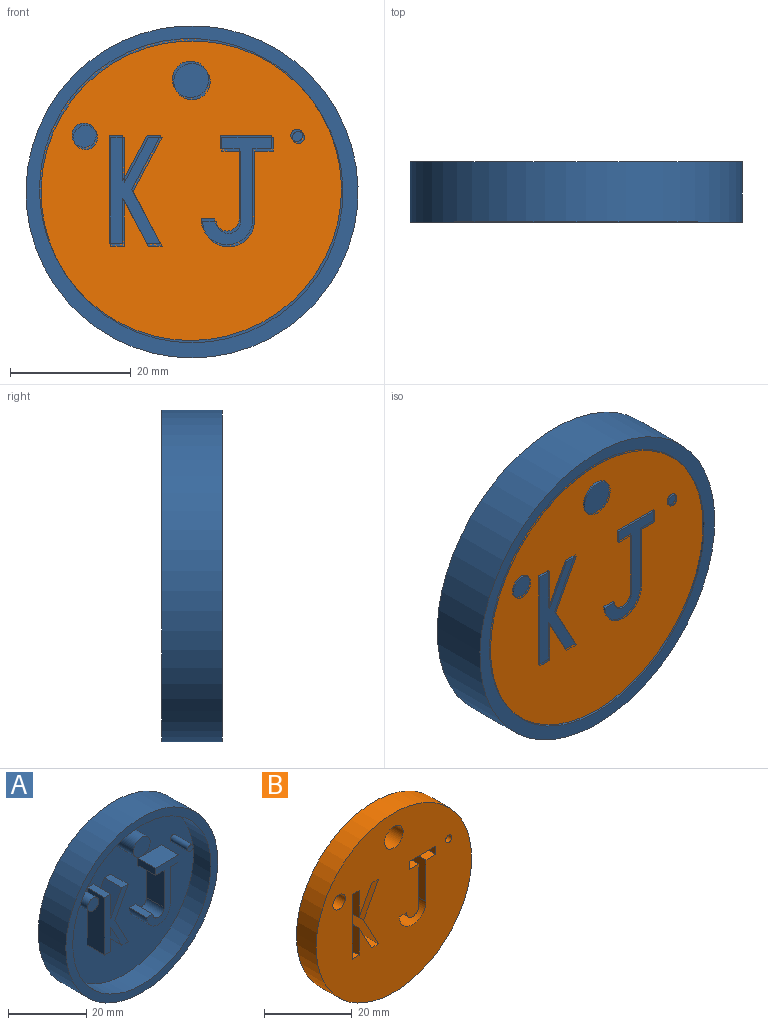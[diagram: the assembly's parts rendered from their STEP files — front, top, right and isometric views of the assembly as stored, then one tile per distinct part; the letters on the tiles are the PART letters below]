
ASSEMBLY  parts=2 mates=1
PART A: 34 faces, bbox 55x10x55 mm
  f0: cylinder r=25mm len=50mm, axis (0,1,0), area 997.5mm2, adj f2,f33
  f1: cylinder r=27.5mm len=55mm, axis (0,1,0), area 1727.9mm2, adj f2,f3
  f2: plane 55x55mm, normal (0,-1,0), area 412.3mm2, adj f0,f1
  f3: plane 55x55mm, normal (0,1,0), area 2375.8mm2, adj f1
  f4: cylinder r=2mm len=6.35mm, axis (0,1,0), area 79.8mm2, adj f5,f33
  f5: plane 4x4mm, normal (0,-1,0), area 12.6mm2, adj f4
  f6: cylinder r=3mm len=6.35mm, axis (0,1,0), area 119.7mm2, adj f7,f33
  f7: plane 6x6mm, normal (0,-1,0), area 28.3mm2, adj f6
  f8: cylinder r=1mm len=6.35mm, axis (0,1,0), area 39.9mm2, adj f9,f33
  f9: plane 2x2mm, normal (0,-1,0), area 3.1mm2, adj f8
  f10: plane 6.35x2.25mm, normal (0,0,1), area 14.3mm2, adj f11,f20,f21,f33
  f11: plane 18x6.35mm, normal (-1,0,0), area 114.3mm2, adj f10,f12,f21,f33
  f12: plane 6.35x2.25mm, normal (0,0,-1), area 14.3mm2, adj f11,f13,f21,f33
  f13: plane 7.5x6.35mm, normal (1,0,0), area 47.6mm2, adj f12,f14,f21,f33
  f14: plane 7.5x6.35mm, normal (-0.88,0,-0.47), area 54mm2, adj f13,f15,f21,f33
  f15: plane 6.35x2.25mm, normal (0,0,-1), area 14.3mm2, adj f14,f16,f21,f33
  f16: plane 9x6.35mm, normal (0.88,0,0.47), area 64.8mm2, adj f15,f17,f21,f33
  f17: plane 9x6.35mm, normal (0.88,0,-0.47), area 64.8mm2, adj f16,f18,f21,f33
  f18: plane 6.35x2.25mm, normal (0,0,1), area 14.3mm2, adj f17,f19,f21,f33
  f19: plane 7.5x6.35mm, normal (-0.88,0,0.47), area 54mm2, adj f18,f20,f21,f33
  f20: plane 7.5x6.35mm, normal (1,0,0), area 47.6mm2, adj f10,f19,f21,f33
  f21: plane 18x8.5mm, normal (0,-1,0), area 79.8mm2, adj f10,f11,f12,f13,f14,f15,f16,f17
  f22: plane 8.5x6.35mm, normal (0,0,1), area 54mm2, adj f23,f31,f32,f33
  f23: plane 6.35x2.25mm, normal (-1,0,0), area 14.3mm2, adj f22,f24,f32,f33
  f24: plane 6.35x3.13mm, normal (0,0,-1), area 19.8mm2, adj f23,f25,f32,f33
  f25: plane 11.6x6.35mm, normal (-1,0,0), area 73.7mm2, adj f24,f26,f32,f33
  f26: cylinder r=2.02mm len=6.35mm, axis (0,1,0), area 40.4mm2, adj f25,f27,f32,f33
  f27: plane 6.35x2.25mm, normal (0,0,1), area 14.3mm2, adj f26,f28,f32,f33
  f28: cylinder r=4.27mm len=8.55mm, axis (0,1,0), area 85.3mm2, adj f27,f29,f32,f33
  f29: plane 11.6x6.35mm, normal (1,0,0), area 73.7mm2, adj f28,f30,f32,f33
  f30: plane 6.35x3.13mm, normal (0,0,-1), area 19.8mm2, adj f29,f31,f32,f33
  f31: plane 6.35x2.25mm, normal (1,0,0), area 14.3mm2, adj f22,f30,f32,f33
  f32: plane 18.13x11.67mm, normal (0,-1,0), area 67.5mm2, adj f22,f23,f24,f25,f26,f27,f28,f29
  f33: plane 50x50mm, normal (0,-1,0), area 1772.2mm2, adj f0,f4,f6,f8,f10,f11,f12,f13
PART B: 27 faces, bbox 50x6.4x50 mm
  f0: plane 6.35x2.25mm, normal (1,0,0), area 14.3mm2, adj f1,f24,f25,f26
  f1: plane 8.5x6.35mm, normal (0,0,-1), area 54mm2, adj f0,f2,f25,f26
  f2: plane 6.35x2.25mm, normal (-1,0,0), area 14.3mm2, adj f1,f3,f25,f26
  f3: plane 6.35x3.13mm, normal (0,0,1), area 19.8mm2, adj f2,f4,f25,f26
  f4: plane 11.6x6.35mm, normal (-1,0,0), area 73.7mm2, adj f3,f5,f25,f26
  f5: cylinder r=4.28mm len=8.55mm, axis (0,1,0), area 85.3mm2, adj f4,f6,f25,f26
  f6: plane 6.35x2.25mm, normal (0,0,-1), area 14.3mm2, adj f5,f7,f25,f26
  f7: cylinder r=2.02mm len=6.35mm, axis (0,1,0), area 40.4mm2, adj f6,f8,f25,f26
  f8: plane 11.6x6.35mm, normal (1,0,0), area 73.7mm2, adj f7,f24,f25,f26
  f9: plane 18x6.35mm, normal (1,0,0), area 114.3mm2, adj f10,f23,f25,f26
  f10: plane 6.35x2.25mm, normal (0,0,-1), area 14.3mm2, adj f9,f11,f25,f26
  f11: plane 7.5x6.35mm, normal (-1,0,0), area 47.6mm2, adj f10,f12,f25,f26
  f12: plane 7.5x6.35mm, normal (0.88,0,-0.47), area 54mm2, adj f11,f13,f25,f26
  f13: plane 6.35x2.25mm, normal (0,0,-1), area 14.3mm2, adj f12,f14,f25,f26
  f14: plane 9x6.35mm, normal (-0.88,0,0.47), area 64.8mm2, adj f13,f15,f25,f26
  f15: plane 9x6.35mm, normal (-0.88,0,-0.47), area 64.8mm2, adj f14,f16,f25,f26
  f16: plane 6.35x2.25mm, normal (0,0,1), area 14.3mm2, adj f15,f17,f25,f26
  f17: plane 7.5x6.35mm, normal (0.88,0,0.47), area 54mm2, adj f16,f18,f25,f26
  f18: plane 7.5x6.35mm, normal (-1,0,0), area 47.6mm2, adj f17,f23,f25,f26
  f19: cylinder r=25mm len=50mm, axis (0,1,0), area 997.5mm2, adj f25,f26
  f20: cylinder r=3mm len=6.35mm, axis (0,1,0), area 119.7mm2, adj f25,f26
  f21: cylinder r=1mm len=6.35mm, axis (0,1,0), area 39.9mm2, adj f25,f26
  f22: cylinder r=2mm len=6.35mm, axis (0,1,0), area 79.8mm2, adj f25,f26
  f23: plane 6.35x2.25mm, normal (0,0,1), area 14.3mm2, adj f9,f18,f25,f26
  f24: plane 6.35x3.13mm, normal (0,0,1), area 19.8mm2, adj f0,f8,f25,f26
  f25: plane 50x50mm, normal (0,-1,0), area 1772.2mm2, adj f0,f1,f2,f3,f4,f5,f6,f7
  f26: plane 50x50mm, normal (0,1,0), area 1772.2mm2, adj f0,f1,f2,f3,f4,f5,f6,f7
PLACE A t=(-9.58,5.19,2.28)mm
PLACE B t=(-9.83,1.54,2.67)mm
MATE slider B.f25 <-> A.f1  axis (0,-1,0) through (-9.58,-4.81,2.28)mm
